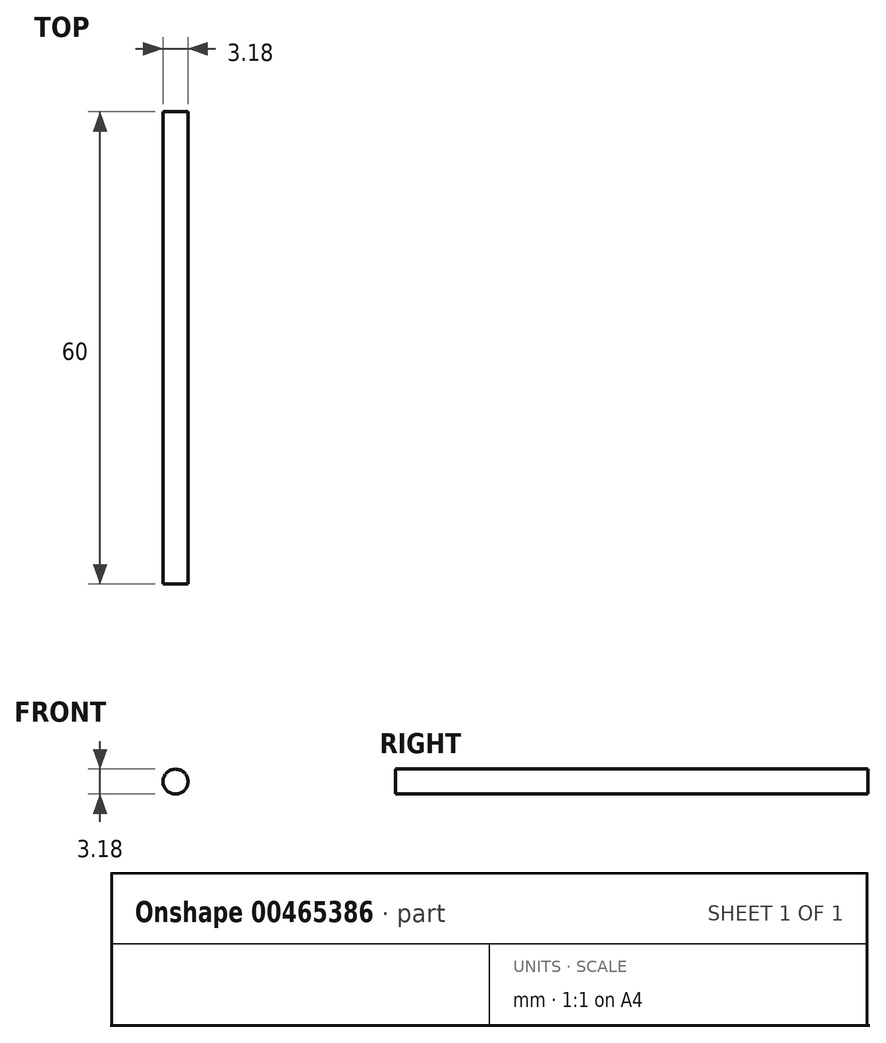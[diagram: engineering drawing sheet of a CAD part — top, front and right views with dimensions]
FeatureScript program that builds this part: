
annotation { "Feature Type Name" : "Feature", "Feature Type Description" : "" }
export const myFeature = defineFeature(function(context is Context, id is Id, definition is map)
    precondition{}
    {
        {
            var Q0;
            Q0=qCreatedBy(makeId("Front.planeOp"),FACE);
            var sketch = newSketch(context, id + "F0", { "sketchPlane" : qUnion([Q0])});
            skCircle(sketch, "E0", {"center": v(0, 0) * mm, "radius": 1.59 * mm});
            skSolve(sketch);
        }
        {
            var Q0;
            Q0=makeQuery(id+"F0.imprint","IMPRINT",FACE,{"disambiguationData":[TD([[makeQuery(id+"F0.imprint","IMPRINT",EDGE,{"derivedFrom":sQuery(id+"F0.wireOp",EDGE,"E0")}),1.0]])]});
            extrude(context, id + "F1", {"entities" : qUnion([Q0]), "depth" : 60 * mm, "offsetDistance" : 25 * mm});
        }
    });
